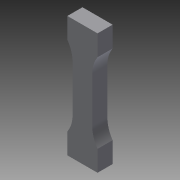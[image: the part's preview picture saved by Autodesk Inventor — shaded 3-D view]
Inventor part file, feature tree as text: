
AUTODESK INVENTOR PART (.ipt)
format: ipt  version: 2014 SP1 (Build 180222100, 222)  size: 86,528 bytes
history: native  units: mm
features: extrude x1, sketch x1
ambient origin geometry x8: Origin, YZ Plane, XZ Plane, XY Plane, X Axis, Y Axis, Z Axis, Center Point
bodies: Solid1 (feature_tree)
feature tree (2):
  extrude  "Extrusion1"  Depth=20.0mm
  sketch  "Sketch1"  dims[d2=20.0mm d5=20.0mm d6=20.0mm d7=40.0mm d8=13.0mm d9=15.0mm d10=10.0mm d11=0.0mm d13=15.0mm]
